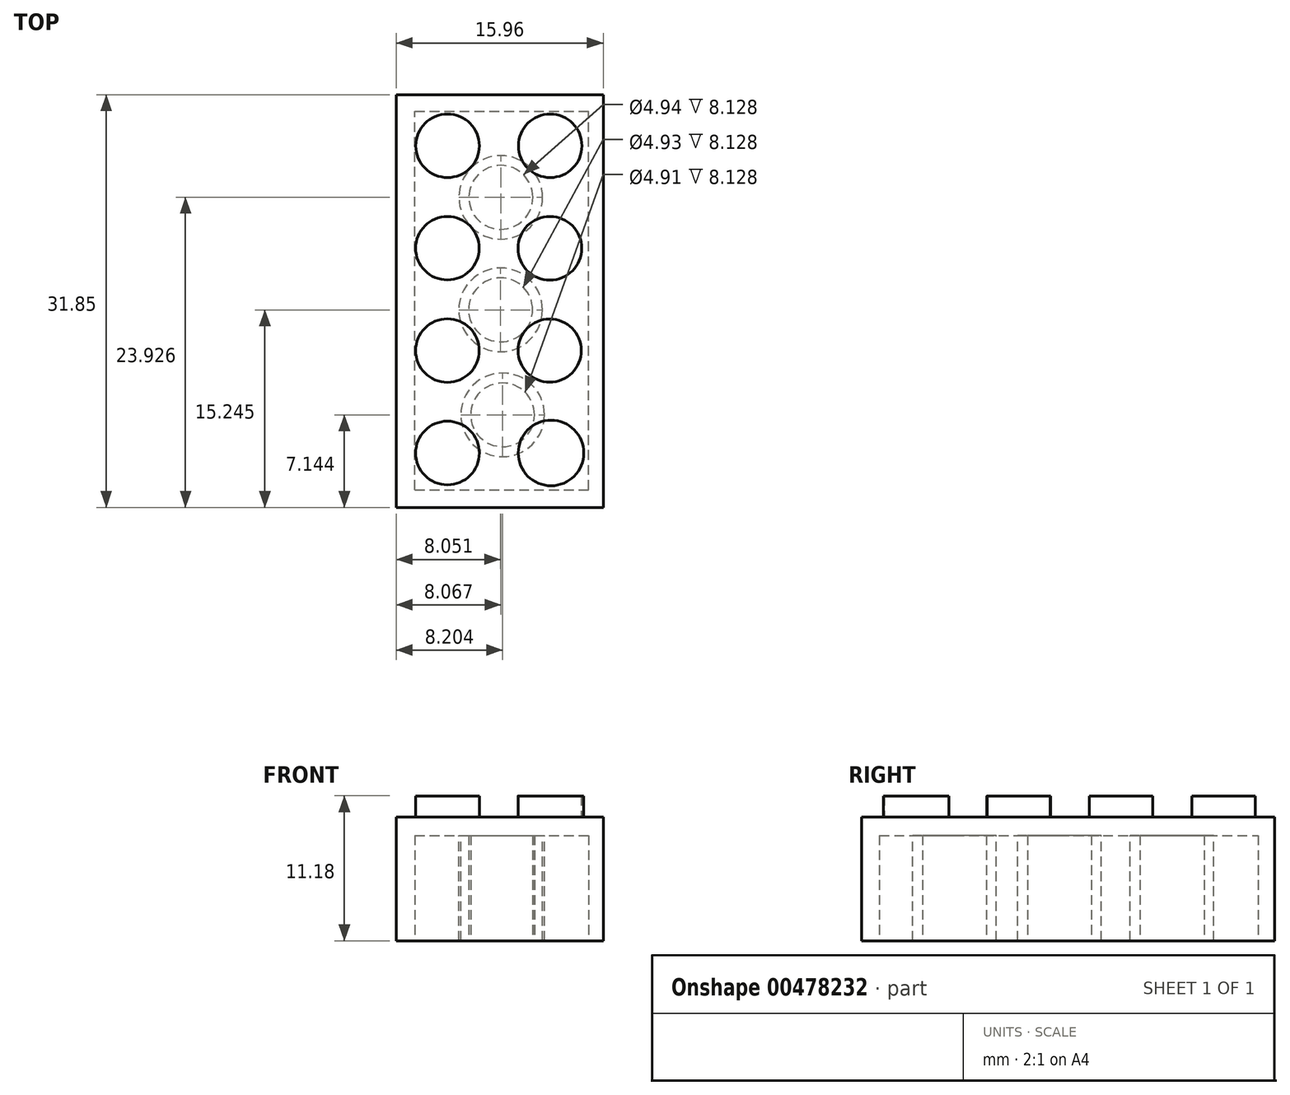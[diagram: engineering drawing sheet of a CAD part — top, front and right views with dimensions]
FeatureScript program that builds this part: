
annotation { "Feature Type Name" : "Feature", "Feature Type Description" : "" }
export const myFeature = defineFeature(function(context is Context, id is Id, definition is map)
    precondition{}
    {
        {
            var Q0;
            Q0=qCreatedBy(makeId("Top.planeOp"),FACE);
            var sketch = newSketch(context, id + "F0", { "sketchPlane" : qUnion([Q0])});
            skLineSegment(sketch, "E0.bottom", {"start": v(-10.65, 9.25) * mm, "end": v(5.31, 9.25) * mm});
            skLineSegment(sketch, "E0.top", {"start": v(-10.65, -22.6) * mm, "end": v(5.31, -22.6) * mm});
            skLineSegment(sketch, "E0.left", {"start": v(-10.65, 9.25) * mm, "end": v(-10.65, -22.6) * mm});
            skLineSegment(sketch, "E0.right", {"start": v(5.31, 9.25) * mm, "end": v(5.31, -22.6) * mm});
            skSolve(sketch);
        }
        {
            var Q0;
            Q0=makeQuery(id+"F0.imprint","IMPRINT",FACE,{"disambiguationData":[TD([[makeQuery(id+"F0.imprint","IMPRINT",EDGE,{"derivedFrom":sQuery(id+"F0.wireOp",EDGE,"E0.bottom")}),-1.0]])]});
            extrude(context, id + "F1", {"entities" : qUnion([Q0]), "depth" : 9.55 * mm});
        }
        {
            var Q0;
            Q0=makeQuery(id+"F1.opExtrude","CAP_FACE",FACE,{"disambiguationData":[OSD([sQuery(id+"F0.wireOp",EDGE,"E0.bottom"),sQuery(id+"F0.wireOp",EDGE,"E0.top"),sQuery(id+"F0.wireOp",EDGE,"E0.left"),sQuery(id+"F0.wireOp",EDGE,"E0.right")])],"isStart":false});
            var sketch = newSketch(context, id + "F2", { "sketchPlane" : qUnion([Q0])});
            skCircle(sketch, "E1", {"center": v(-6.7, 5.3) * mm, "radius": 2.45 * mm});
            skCircle(sketch, "E2", {"center": v(1.22, 5.3) * mm, "radius": 2.45 * mm});
            skCircle(sketch, "E3", {"center": v(-6.7, -2.6) * mm, "radius": 2.45 * mm});
            skCircle(sketch, "E4", {"center": v(1.2, -2.6) * mm, "radius": 2.46 * mm});
            skCircle(sketch, "E5", {"center": v(-6.7, -10.5) * mm, "radius": 2.45 * mm});
            skCircle(sketch, "E6", {"center": v(1.19, -10.5) * mm, "radius": 2.44 * mm});
            skCircle(sketch, "E7", {"center": v(-6.7, -18.4) * mm, "radius": 2.46 * mm});
            skCircle(sketch, "E8", {"center": v(1.28, -18.4) * mm, "radius": 2.53 * mm});
            skSolve(sketch);
        }
        {
            var Q0;
            Q0 = qSketchRegion(id + "F2", true);
            extrude(context, id + "F3", {"entities" : qUnion([Q0]), "operationType" : NewBodyOperationType.ADD, "depth" : 1.63 * mm});
        }
        {
            var Q0;
            Q0=makeQuery(id+"F1.opExtrude","CAP_FACE",FACE,{"disambiguationData":[OSD([sQuery(id+"F0.wireOp",EDGE,"E0.bottom"),sQuery(id+"F0.wireOp",EDGE,"E0.top"),sQuery(id+"F0.wireOp",EDGE,"E0.left"),sQuery(id+"F0.wireOp",EDGE,"E0.right")])],"isStart":true});
            var sketch = newSketch(context, id + "F4", { "sketchPlane" : qUnion([Q0])});
            skLineSegment(sketch, "E9.bottom", {"start": v(-9.22, 21.23) * mm, "end": v(4.17, 21.23) * mm});
            skLineSegment(sketch, "E9.top", {"start": v(-9.22, -7.98) * mm, "end": v(4.17, -7.98) * mm});
            skLineSegment(sketch, "E9.left", {"start": v(-9.22, 21.23) * mm, "end": v(-9.22, -7.98) * mm});
            skLineSegment(sketch, "E9.right", {"start": v(4.17, 21.23) * mm, "end": v(4.17, -7.98) * mm});
            skSolve(sketch);
        }
        {
            var Q0;
            Q0=makeQuery(id+"F4.imprint","IMPRINT",FACE,{"disambiguationData":[TD([[makeQuery(id+"F4.imprint","IMPRINT",EDGE,{"derivedFrom":sQuery(id+"F4.wireOp",EDGE,"E9.bottom")}),-1.0]])]});
            extrude(context, id + "F5", {"entities" : qUnion([Q0]), "operationType" : NewBodyOperationType.REMOVE, "oppositeDirection" : true, "depth" : 8.13 * mm});
        }
        {
            var Q0;
            Q0=makeQuery(id+"F5.boolean.opBoolean","COPY",FACE,{"derivedFrom":makeQuery(id+"F5.opExtrude","CAP_FACE",FACE,{"disambiguationData":[OSD([sQuery(id+"F4.wireOp",EDGE,"E9.bottom"),sQuery(id+"F4.wireOp",EDGE,"E9.top"),sQuery(id+"F4.wireOp",EDGE,"E9.left"),sQuery(id+"F4.wireOp",EDGE,"E9.right")])],"isStart":false})});
            var sketch = newSketch(context, id + "F6", { "sketchPlane" : qUnion([Q0])});
            skCircle(sketch, "E10", {"center": v(-2.45, 15.46) * mm, "radius": 3.23 * mm});
            skCircle(sketch, "E11", {"center": v(-2.6, 7.36) * mm, "radius": 3.23 * mm});
            skCircle(sketch, "E12", {"center": v(-2.59, -1.32) * mm, "radius": 3.23 * mm});
            skSolve(sketch);
        }
        {
            var Q0;
            Q0=makeQuery(id+"F6.imprint","IMPRINT",FACE,{"disambiguationData":[TD([[makeQuery(id+"F6.imprint","IMPRINT",EDGE,{"derivedFrom":sQuery(id+"F6.wireOp",EDGE,"E10")}),1.0]])]});
            var Q1;
            Q1=makeQuery(id+"F6.imprint","IMPRINT",FACE,{"disambiguationData":[TD([[makeQuery(id+"F6.imprint","IMPRINT",EDGE,{"derivedFrom":sQuery(id+"F6.wireOp",EDGE,"E11")}),1.0]])]});
            var Q2;
            Q2=makeQuery(id+"F6.imprint","IMPRINT",FACE,{"disambiguationData":[TD([[makeQuery(id+"F6.imprint","IMPRINT",EDGE,{"derivedFrom":sQuery(id+"F6.wireOp",EDGE,"E12")}),1.0]])]});
            extrude(context, id + "F7", {"entities" : qUnion([Q0, Q1, Q2]), "operationType" : NewBodyOperationType.ADD, "depth" : 8.13 * mm});
        }
        {
            var Q0;
            Q0=makeQuery(id+"F7.opExtrude","CAP_FACE",FACE,{"disambiguationData":[OSD([sQuery(id+"F6.wireOp",EDGE,"E10")])],"isStart":false});
            var sketch = newSketch(context, id + "F8", { "sketchPlane" : qUnion([Q0])});
            skCircle(sketch, "E13", {"center": v(-2.45, 15.46) * mm, "radius": 2.46 * mm});
            skCircle(sketch, "E14", {"center": v(-2.6, 7.36) * mm, "radius": 2.46 * mm});
            skCircle(sketch, "E15", {"center": v(-2.58, -1.33) * mm, "radius": 2.47 * mm});
            skSolve(sketch);
        }
        {
            var Q0;
            Q0=makeQuery(id+"F8.imprint","IMPRINT",FACE,{"disambiguationData":[TD([[makeQuery(id+"F8.imprint","IMPRINT",EDGE,{"derivedFrom":sQuery(id+"F8.wireOp",EDGE,"E13")}),1.0]])]});
            var Q1;
            Q1=makeQuery(id+"F8.imprint","IMPRINT",FACE,{"disambiguationData":[TD([[makeQuery(id+"F8.imprint","IMPRINT",EDGE,{"derivedFrom":sQuery(id+"F8.wireOp",EDGE,"E14")}),1.0]])]});
            var Q2;
            Q2=makeQuery(id+"F8.imprint","IMPRINT",FACE,{"disambiguationData":[TD([[makeQuery(id+"F8.imprint","IMPRINT",EDGE,{"derivedFrom":sQuery(id+"F8.wireOp",EDGE,"E15")}),1.0]])]});
            extrude(context, id + "F9", {"entities" : qUnion([Q0, Q1, Q2]), "operationType" : NewBodyOperationType.REMOVE, "oppositeDirection" : true, "depth" : 8.13 * mm});
        }
    });
